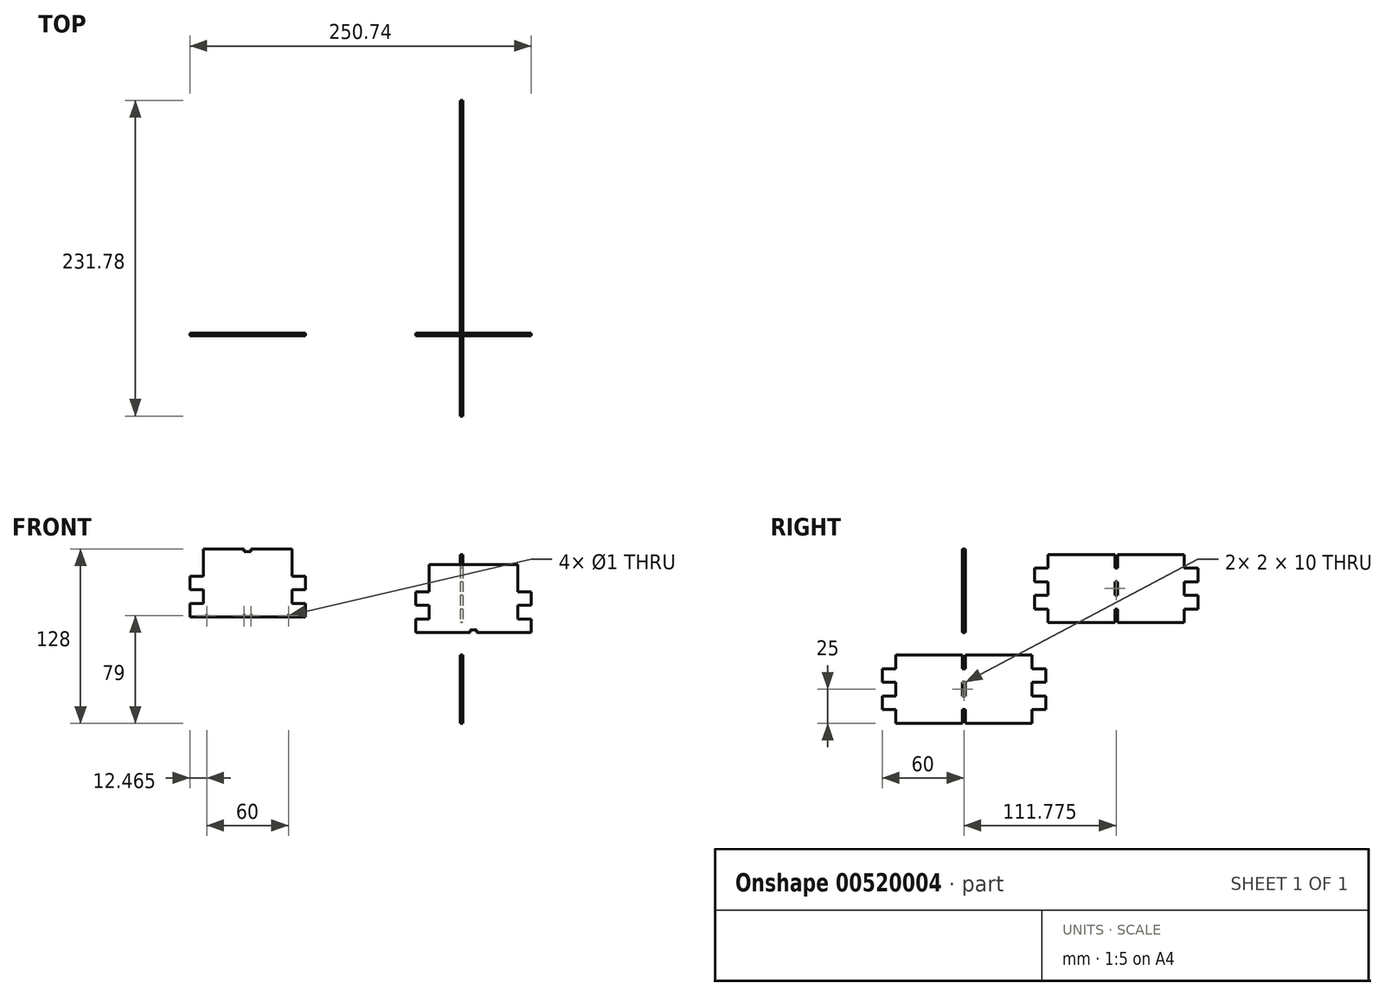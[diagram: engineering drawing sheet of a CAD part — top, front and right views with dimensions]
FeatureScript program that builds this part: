
annotation { "Feature Type Name" : "Feature", "Feature Type Description" : "" }
export const myFeature = defineFeature(function(context is Context, id is Id, definition is map)
    precondition{}
    {
        {
            var Q0;
            Q0=qCreatedBy(makeId("Front.planeOp"),FACE);
            var sketch = newSketch(context, id + "F0", { "sketchPlane" : qUnion([Q0])});
            skLineSegment(sketch, "E0.bottom", {"start": v(-198.62, 60.37) * mm, "end": v(-113.65, 60.37) * mm});
            skLineSegment(sketch, "E0.top", {"start": v(-198.62, 10.37) * mm, "end": v(-113.65, 10.37) * mm});
            skLineSegment(sketch, "E0.left", {"start": v(-198.62, 60.37) * mm, "end": v(-198.62, 10.37) * mm});
            skLineSegment(sketch, "E0.right", {"start": v(-113.65, 60.37) * mm, "end": v(-113.65, 10.37) * mm});
            skLineSegment(sketch, "E1.bottom", {"start": v(-198.62, 60.37) * mm, "end": v(-188.65, 60.37) * mm});
            skLineSegment(sketch, "E1.top", {"start": v(-198.62, 50.37) * mm, "end": v(-188.65, 50.37) * mm});
            skLineSegment(sketch, "E1.left", {"start": v(-198.62, 60.37) * mm, "end": v(-198.62, 50.37) * mm});
            skLineSegment(sketch, "E1.right", {"start": v(-188.65, 60.37) * mm, "end": v(-188.65, 50.37) * mm});
            skLineSegment(sketch, "E2.0.1.0", {"start": v(-198.62, 40.37) * mm, "end": v(-188.65, 40.37) * mm});
            skLineSegment(sketch, "E2.0.1.1", {"start": v(-198.62, 40.37) * mm, "end": v(-198.62, 30.37) * mm});
            skLineSegment(sketch, "E2.0.1.2", {"start": v(-188.65, 40.37) * mm, "end": v(-188.65, 30.37) * mm});
            skLineSegment(sketch, "E2.0.1.3", {"start": v(-198.62, 30.37) * mm, "end": v(-188.65, 30.37) * mm});
            skLineSegment(sketch, "E2.0.2.0", {"start": v(-198.62, 20.37) * mm, "end": v(-188.65, 20.37) * mm});
            skLineSegment(sketch, "E2.0.2.1", {"start": v(-198.62, 20.37) * mm, "end": v(-198.62, 10.37) * mm});
            skLineSegment(sketch, "E2.0.2.2", {"start": v(-188.65, 20.37) * mm, "end": v(-188.65, 10.37) * mm});
            skLineSegment(sketch, "E2.0.2.3", {"start": v(-198.62, 10.37) * mm, "end": v(-188.65, 10.37) * mm});
            skLineSegment(sketch, "E2.direction2", {"start": v(-198.62, 50.37) * mm, "end": v(-198.62, 30.37) * mm, "construction": true});
            skLineSegment(sketch, "E3.bottom", {"start": v(-113.65, 60.37) * mm, "end": v(-123.65, 60.37) * mm});
            skLineSegment(sketch, "E3.top", {"start": v(-113.65, 50.37) * mm, "end": v(-123.65, 50.37) * mm});
            skLineSegment(sketch, "E3.left", {"start": v(-113.65, 60.37) * mm, "end": v(-113.65, 50.37) * mm});
            skLineSegment(sketch, "E3.right", {"start": v(-123.65, 60.37) * mm, "end": v(-123.65, 50.37) * mm});
            skLineSegment(sketch, "E4.0.1.0", {"start": v(-123.65, 40.37) * mm, "end": v(-123.65, 30.37) * mm});
            skLineSegment(sketch, "E4.0.1.1", {"start": v(-113.65, 40.37) * mm, "end": v(-123.65, 40.37) * mm});
            skLineSegment(sketch, "E4.0.1.2", {"start": v(-113.65, 30.37) * mm, "end": v(-123.65, 30.37) * mm});
            skLineSegment(sketch, "E4.0.1.3", {"start": v(-113.65, 40.37) * mm, "end": v(-113.65, 30.37) * mm});
            skLineSegment(sketch, "E4.0.2.0", {"start": v(-123.65, 20.37) * mm, "end": v(-123.65, 10.37) * mm});
            skLineSegment(sketch, "E4.0.2.1", {"start": v(-113.65, 20.37) * mm, "end": v(-123.65, 20.37) * mm});
            skLineSegment(sketch, "E4.0.2.2", {"start": v(-113.65, 10.37) * mm, "end": v(-123.65, 10.37) * mm});
            skLineSegment(sketch, "E4.0.2.3", {"start": v(-113.65, 20.37) * mm, "end": v(-113.65, 10.37) * mm});
            skLineSegment(sketch, "E4.direction2", {"start": v(-123.65, 50.37) * mm, "end": v(-123.65, 30.37) * mm});
            skLineSegment(sketch, "E5", {"start": v(-188.65, 50.37) * mm, "end": v(-188.65, 40.37) * mm});
            skLineSegment(sketch, "E6", {"start": v(-188.65, 30.37) * mm, "end": v(-188.65, 20.37) * mm});
            skLineSegment(sketch, "E7", {"start": v(-123.65, 20.37) * mm, "end": v(-123.65, 30.37) * mm});
            skCircle(sketch, "E8", {"center": v(-186.15, 11.37) * mm, "radius": 0.5 * mm});
            skCircle(sketch, "E9.1.0.0", {"center": v(-158.65, 11.37) * mm, "radius": 0.5 * mm});
            skCircle(sketch, "E9.2.0.0", {"center": v(-153.65, 11.37) * mm, "radius": 0.5 * mm});
            skCircle(sketch, "E10.1.0.0", {"center": v(-126.15, 11.37) * mm, "radius": 0.5 * mm});
            skLineSegment(sketch, "E11.bottom", {"start": v(-158.65, 60.37) * mm, "end": v(-153.65, 60.37) * mm});
            skLineSegment(sketch, "E11.top", {"start": v(-158.65, 58.37) * mm, "end": v(-153.65, 58.37) * mm});
            skLineSegment(sketch, "E11.left", {"start": v(-158.65, 60.37) * mm, "end": v(-158.65, 58.37) * mm});
            skLineSegment(sketch, "E11.right", {"start": v(-153.65, 60.37) * mm, "end": v(-153.65, 58.37) * mm});
            skSolve(sketch);
        }
        {
            var Q0;
            Q0=makeQuery(id+"F0.imprint","IMPRINT",FACE,{"disambiguationData":[TD([[makeQuery(id+"F0.imprint","IMPRINT",EDGE,{"derivedFrom":sQuery(id+"F0.wireOp",EDGE,"E1.bottom")}),-1.0]])]});
            var Q1;
            Q1=makeQuery(id+"F0.imprint","IMPRINT",FACE,{"disambiguationData":[TD([[makeQuery(id+"F0.imprint","IMPRINT",EDGE,{"derivedFrom":sQuery(id+"F0.wireOp",EDGE,"E2.0.1.0")}),-1.0]])]});
            var Q2;
            Q2=makeQuery(id+"F0.imprint","IMPRINT",FACE,{"disambiguationData":[TD([[makeQuery(id+"F0.imprint","IMPRINT",EDGE,{"derivedFrom":sQuery(id+"F0.wireOp",EDGE,"E2.0.2.0")}),-1.0]])]});
            var Q3;
            Q3=makeQuery(id+"F0.imprint","IMPRINT",FACE,{"disambiguationData":[TD([[makeQuery(id+"F0.imprint","IMPRINT",EDGE,{"derivedFrom":sQuery(id+"F0.wireOp",EDGE,"E3.bottom")}),1.0]])]});
            var Q4;
            {var subQ0=sQuery(id+"F0.wireOp",EDGE,"E4.0.1.1");Q4=makeQuery(id+"F0.imprint","IMPRINT",FACE,{"disambiguationData":[TD([[makeQuery(id+"F0.imprint","IMPRINT",EDGE,{"derivedFrom":subQ0}),1.0]])]});}
            var Q5;
            Q5=makeQuery(id+"F0.imprint","IMPRINT",FACE,{"disambiguationData":[TD([[makeQuery(id+"F0.imprint","IMPRINT",EDGE,{"derivedFrom":sQuery(id+"F0.wireOp",EDGE,"E4.0.2.0")}),1.0]])]});
            var Q6;
            {var subQ6=sQuery(id+"F0.wireOp",EDGE,"E1.right");Q6=makeQuery(id+"F0.imprint","IMPRINT",FACE,{"disambiguationData":[TD([[makeQuery(id+"F0.imprint","IMPRINT",EDGE,{"derivedFrom":subQ6}),1.0]])]});}
            var Q7;
            Q7=makeQuery(id+"F0.imprint","IMPRINT",FACE,{"disambiguationData":[TD([[makeQuery(id+"F0.imprint","IMPRINT",EDGE,{"derivedFrom":sQuery(id+"F0.wireOp",EDGE,"E11.bottom")}),-1.0]])]});
            extrude(context, id + "F1", {"entities" : qUnion([Q0, Q1, Q2, Q3, Q4, Q5, Q6, Q7]), "depth" : 2 * mm, "offsetDistance" : 25 * mm});
        }
        {
            var Q0;
            Q0=qCreatedBy(makeId("Front.planeOp"),FACE);
            var sketch = newSketch(context, id + "F2", { "sketchPlane" : qUnion([Q0])});
            skLineSegment(sketch, "E12.bottom", {"start": v(-32.85, 48.9) * mm, "end": v(52.12, 48.9) * mm});
            skLineSegment(sketch, "E12.top", {"start": v(-32.85, -1.1) * mm, "end": v(52.12, -1.1) * mm});
            skLineSegment(sketch, "E12.left", {"start": v(-32.85, 48.9) * mm, "end": v(-32.85, -1.1) * mm});
            skLineSegment(sketch, "E12.right", {"start": v(52.12, 48.9) * mm, "end": v(52.12, -1.1) * mm});
            skLineSegment(sketch, "E13.bottom", {"start": v(-32.85, 48.9) * mm, "end": v(-22.88, 48.9) * mm});
            skLineSegment(sketch, "E13.top", {"start": v(-32.85, 38.9) * mm, "end": v(-22.88, 38.9) * mm});
            skLineSegment(sketch, "E13.left", {"start": v(-32.85, 48.9) * mm, "end": v(-32.85, 38.9) * mm});
            skLineSegment(sketch, "E13.right", {"start": v(-22.88, 48.9) * mm, "end": v(-22.88, 38.9) * mm});
            skLineSegment(sketch, "E14.0.1.0", {"start": v(-32.85, 28.9) * mm, "end": v(-22.88, 28.9) * mm});
            skLineSegment(sketch, "E14.0.1.1", {"start": v(-32.85, 28.9) * mm, "end": v(-32.85, 18.9) * mm});
            skLineSegment(sketch, "E14.0.1.2", {"start": v(-22.88, 28.9) * mm, "end": v(-22.88, 18.9) * mm});
            skLineSegment(sketch, "E14.0.1.3", {"start": v(-32.85, 18.9) * mm, "end": v(-22.88, 18.9) * mm});
            skLineSegment(sketch, "E14.0.2.0", {"start": v(-32.85, 8.9) * mm, "end": v(-22.88, 8.9) * mm});
            skLineSegment(sketch, "E14.0.2.1", {"start": v(-32.85, 8.9) * mm, "end": v(-32.85, -1.1) * mm});
            skLineSegment(sketch, "E14.0.2.2", {"start": v(-22.88, 8.9) * mm, "end": v(-22.88, -1.1) * mm});
            skLineSegment(sketch, "E14.0.2.3", {"start": v(-32.85, -1.1) * mm, "end": v(-22.88, -1.1) * mm});
            skLineSegment(sketch, "E14.direction2", {"start": v(-32.85, 38.9) * mm, "end": v(-32.85, 18.9) * mm, "construction": true});
            skLineSegment(sketch, "E15.bottom", {"start": v(52.12, 48.9) * mm, "end": v(42.12, 48.9) * mm});
            skLineSegment(sketch, "E15.top", {"start": v(52.12, 38.9) * mm, "end": v(42.12, 38.9) * mm});
            skLineSegment(sketch, "E15.left", {"start": v(52.12, 48.9) * mm, "end": v(52.12, 38.9) * mm});
            skLineSegment(sketch, "E15.right", {"start": v(42.12, 48.9) * mm, "end": v(42.12, 38.9) * mm});
            skLineSegment(sketch, "E16.0.1.0", {"start": v(42.12, 28.9) * mm, "end": v(42.12, 18.9) * mm});
            skLineSegment(sketch, "E16.0.1.1", {"start": v(52.12, 28.9) * mm, "end": v(42.12, 28.9) * mm});
            skLineSegment(sketch, "E16.0.1.2", {"start": v(52.12, 18.9) * mm, "end": v(42.12, 18.9) * mm});
            skLineSegment(sketch, "E16.0.1.3", {"start": v(52.12, 28.9) * mm, "end": v(52.12, 18.9) * mm});
            skLineSegment(sketch, "E16.0.2.0", {"start": v(42.12, 8.9) * mm, "end": v(42.12, -1.1) * mm});
            skLineSegment(sketch, "E16.0.2.1", {"start": v(52.12, 8.9) * mm, "end": v(42.12, 8.9) * mm});
            skLineSegment(sketch, "E16.0.2.2", {"start": v(52.12, -1.1) * mm, "end": v(42.12, -1.1) * mm});
            skLineSegment(sketch, "E16.0.2.3", {"start": v(52.12, 8.9) * mm, "end": v(52.12, -1.1) * mm});
            skLineSegment(sketch, "E16.direction2", {"start": v(42.12, 38.9) * mm, "end": v(42.12, 18.9) * mm});
            skLineSegment(sketch, "E17", {"start": v(-22.88, 38.9) * mm, "end": v(-22.88, 28.9) * mm});
            skLineSegment(sketch, "E18", {"start": v(-22.88, 18.9) * mm, "end": v(-22.88, 8.9) * mm});
            skLineSegment(sketch, "E19", {"start": v(42.12, 8.9) * mm, "end": v(42.12, 18.9) * mm});
            skCircle(sketch, "E20", {"center": v(-20.38, 3.9) * mm, "radius": 0.5 * mm});
            skCircle(sketch, "E21.1.0.0", {"center": v(7.12, 3.9) * mm, "radius": 0.5 * mm});
            skCircle(sketch, "E21.2.0.0", {"center": v(12.12, 3.9) * mm, "radius": 0.5 * mm});
            skCircle(sketch, "E22.1.0.0", {"center": v(39.62, 3.9) * mm, "radius": 0.5 * mm});
            skLineSegment(sketch, "E23.bottom", {"start": v(7.12, 48.9) * mm, "end": v(12.12, 48.9) * mm});
            skLineSegment(sketch, "E24.bottom", {"start": v(7.12, 0.9) * mm, "end": v(12.12, 0.9) * mm});
            skLineSegment(sketch, "E24.top", {"start": v(7.12, -1.1) * mm, "end": v(12.12, -1.1) * mm});
            skLineSegment(sketch, "E24.left", {"start": v(7.12, 0.9) * mm, "end": v(7.12, -1.1) * mm});
            skLineSegment(sketch, "E24.right", {"start": v(12.12, 0.9) * mm, "end": v(12.12, -1.1) * mm});
            skSolve(sketch);
        }
        {
            var Q0;
            {var subQ6=sQuery(id+"F2.wireOp",EDGE,"E13.right");Q0=makeQuery(id+"F2.imprint","IMPRINT",FACE,{"disambiguationData":[TD([[makeQuery(id+"F2.imprint","IMPRINT",EDGE,{"derivedFrom":subQ6}),1.0]])]});}
            var Q1;
            Q1=makeQuery(id+"F2.imprint","IMPRINT",FACE,{"disambiguationData":[TD([[makeQuery(id+"F2.imprint","IMPRINT",EDGE,{"derivedFrom":sQuery(id+"F2.wireOp",EDGE,"E15.bottom")}),1.0]])]});
            var Q2;
            {var subQ0=sQuery(id+"F2.wireOp",EDGE,"E16.0.1.1");Q2=makeQuery(id+"F2.imprint","IMPRINT",FACE,{"disambiguationData":[TD([[makeQuery(id+"F2.imprint","IMPRINT",EDGE,{"derivedFrom":subQ0}),1.0]])]});}
            var Q3;
            Q3=makeQuery(id+"F2.imprint","IMPRINT",FACE,{"disambiguationData":[TD([[makeQuery(id+"F2.imprint","IMPRINT",EDGE,{"derivedFrom":sQuery(id+"F2.wireOp",EDGE,"E16.0.2.0")}),1.0]])]});
            var Q4;
            Q4=makeQuery(id+"F2.imprint","IMPRINT",FACE,{"disambiguationData":[TD([[makeQuery(id+"F2.imprint","IMPRINT",EDGE,{"derivedFrom":sQuery(id+"F2.wireOp",EDGE,"E13.bottom")}),-1.0]])]});
            var Q5;
            Q5=makeQuery(id+"F2.imprint","IMPRINT",FACE,{"disambiguationData":[TD([[makeQuery(id+"F2.imprint","IMPRINT",EDGE,{"derivedFrom":sQuery(id+"F2.wireOp",EDGE,"E14.0.1.0")}),-1.0]])]});
            var Q6;
            Q6=makeQuery(id+"F2.imprint","IMPRINT",FACE,{"disambiguationData":[TD([[makeQuery(id+"F2.imprint","IMPRINT",EDGE,{"derivedFrom":sQuery(id+"F2.wireOp",EDGE,"E14.0.2.0")}),-1.0]])]});
            var Q7;
            Q7=makeQuery(id+"F2.imprint","IMPRINT",FACE,{"disambiguationData":[TD([[makeQuery(id+"F2.imprint","IMPRINT",EDGE,{"derivedFrom":sQuery(id+"F2.wireOp",EDGE,"E20")}),1.0]])]});
            var Q8;
            Q8=makeQuery(id+"F2.imprint","IMPRINT",FACE,{"disambiguationData":[TD([[makeQuery(id+"F2.imprint","IMPRINT",EDGE,{"derivedFrom":sQuery(id+"F2.wireOp",EDGE,"E21.1.0.0")}),1.0]])]});
            var Q9;
            Q9=makeQuery(id+"F2.imprint","IMPRINT",FACE,{"disambiguationData":[TD([[makeQuery(id+"F2.imprint","IMPRINT",EDGE,{"derivedFrom":sQuery(id+"F2.wireOp",EDGE,"E21.2.0.0")}),1.0]])]});
            var Q10;
            Q10=makeQuery(id+"F2.imprint","IMPRINT",FACE,{"disambiguationData":[TD([[makeQuery(id+"F2.imprint","IMPRINT",EDGE,{"derivedFrom":sQuery(id+"F2.wireOp",EDGE,"E22.1.0.0")}),1.0]])]});
            extrude(context, id + "F3", {"entities" : qUnion([Q0, Q1, Q2, Q3, Q4, Q5, Q6, Q7, Q8, Q9, Q10]), "depth" : 2 * mm, "offsetDistance" : 25 * mm});
        }
        {
            var Q0;
            Q0=qCreatedBy(makeId("Right.planeOp"),FACE);
            var sketch = newSketch(context, id + "F4", { "sketchPlane" : qUnion([Q0])});
            skLineSegment(sketch, "E25.bottom", {"start": v(-51, -17.63) * mm, "end": v(49, -17.63) * mm});
            skLineSegment(sketch, "E25.top", {"start": v(-51, -67.63) * mm, "end": v(49, -67.63) * mm});
            skLineSegment(sketch, "E25.left", {"start": v(-51, -17.63) * mm, "end": v(-51, -67.63) * mm});
            skLineSegment(sketch, "E25.right", {"start": v(49, -17.63) * mm, "end": v(49, -67.63) * mm});
            skLineSegment(sketch, "E26.bottom", {"start": v(-2, -17.63) * mm, "end": v(0, -17.63) * mm});
            skLineSegment(sketch, "E26.top", {"start": v(-2, -27.63) * mm, "end": v(0, -27.63) * mm});
            skLineSegment(sketch, "E26.left", {"start": v(-2, -17.63) * mm, "end": v(-2, -27.63) * mm});
            skLineSegment(sketch, "E26.right", {"start": v(0, -17.63) * mm, "end": v(0, -27.63) * mm});
            skLineSegment(sketch, "E27.0.1.0", {"start": v(-2, -47.63) * mm, "end": v(0, -47.63) * mm});
            skLineSegment(sketch, "E27.0.1.1", {"start": v(-2, -37.63) * mm, "end": v(-2, -47.63) * mm});
            skLineSegment(sketch, "E27.0.1.2", {"start": v(0, -37.63) * mm, "end": v(0, -47.63) * mm});
            skLineSegment(sketch, "E27.0.1.3", {"start": v(-2, -37.63) * mm, "end": v(0, -37.63) * mm});
            skLineSegment(sketch, "E27.0.2.0", {"start": v(-2, -67.63) * mm, "end": v(0, -67.63) * mm});
            skLineSegment(sketch, "E27.0.2.1", {"start": v(-2, -57.63) * mm, "end": v(-2, -67.63) * mm});
            skLineSegment(sketch, "E27.0.2.2", {"start": v(0, -57.63) * mm, "end": v(0, -67.63) * mm});
            skLineSegment(sketch, "E27.0.2.3", {"start": v(-2, -57.63) * mm, "end": v(0, -57.63) * mm});
            skLineSegment(sketch, "E27.direction1", {"start": v(-2, -27.63) * mm, "end": v(-0.14, -27.63) * mm, "construction": true});
            skLineSegment(sketch, "E28.bottom", {"start": v(49, -17.63) * mm, "end": v(59, -17.63) * mm});
            skLineSegment(sketch, "E28.top", {"start": v(49, -27.63) * mm, "end": v(59, -27.63) * mm});
            skLineSegment(sketch, "E28.left", {"start": v(49, -17.63) * mm, "end": v(49, -27.63) * mm});
            skLineSegment(sketch, "E28.right", {"start": v(59, -17.63) * mm, "end": v(59, -27.63) * mm});
            skLineSegment(sketch, "E29.0.1.0", {"start": v(59, -37.63) * mm, "end": v(59, -47.63) * mm});
            skLineSegment(sketch, "E29.0.1.1", {"start": v(49, -47.63) * mm, "end": v(59, -47.63) * mm});
            skLineSegment(sketch, "E29.0.1.2", {"start": v(49, -37.63) * mm, "end": v(49, -47.63) * mm});
            skLineSegment(sketch, "E29.0.1.3", {"start": v(49, -37.63) * mm, "end": v(59, -37.63) * mm});
            skLineSegment(sketch, "E29.0.2.0", {"start": v(59, -57.63) * mm, "end": v(59, -67.63) * mm});
            skLineSegment(sketch, "E29.0.2.1", {"start": v(49, -67.63) * mm, "end": v(59, -67.63) * mm});
            skLineSegment(sketch, "E29.0.2.2", {"start": v(49, -57.63) * mm, "end": v(49, -67.63) * mm});
            skLineSegment(sketch, "E29.0.2.3", {"start": v(49, -57.63) * mm, "end": v(59, -57.63) * mm});
            skLineSegment(sketch, "E29.direction2", {"start": v(49, -27.63) * mm, "end": v(49, -47.63) * mm, "construction": true});
            skLineSegment(sketch, "E30.bottom", {"start": v(-51, -17.63) * mm, "end": v(-61, -17.63) * mm});
            skLineSegment(sketch, "E30.top", {"start": v(-51, -27.63) * mm, "end": v(-61, -27.63) * mm});
            skLineSegment(sketch, "E30.left", {"start": v(-51, -17.63) * mm, "end": v(-51, -27.63) * mm});
            skLineSegment(sketch, "E30.right", {"start": v(-61, -17.63) * mm, "end": v(-61, -27.63) * mm});
            skLineSegment(sketch, "E31.0.1.0", {"start": v(-51, -37.63) * mm, "end": v(-51, -47.63) * mm});
            skLineSegment(sketch, "E31.0.1.1", {"start": v(-51, -47.63) * mm, "end": v(-61, -47.63) * mm});
            skLineSegment(sketch, "E31.0.1.2", {"start": v(-51, -37.63) * mm, "end": v(-61, -37.63) * mm});
            skLineSegment(sketch, "E31.0.1.3", {"start": v(-61, -37.63) * mm, "end": v(-61, -47.63) * mm});
            skLineSegment(sketch, "E31.0.2.0", {"start": v(-51, -57.63) * mm, "end": v(-51, -67.63) * mm});
            skLineSegment(sketch, "E31.0.2.1", {"start": v(-51, -67.63) * mm, "end": v(-61, -67.63) * mm});
            skLineSegment(sketch, "E31.0.2.2", {"start": v(-51, -57.63) * mm, "end": v(-61, -57.63) * mm});
            skLineSegment(sketch, "E31.0.2.3", {"start": v(-61, -57.63) * mm, "end": v(-61, -67.63) * mm});
            skLineSegment(sketch, "E32", {"start": v(-61, -27.63) * mm, "end": v(-61, -37.63) * mm});
            skLineSegment(sketch, "E33", {"start": v(-61, -47.63) * mm, "end": v(-61, -57.63) * mm});
            skLineSegment(sketch, "E34", {"start": v(59, -27.63) * mm, "end": v(59, -37.63) * mm});
            skLineSegment(sketch, "E35", {"start": v(59, -47.63) * mm, "end": v(59, -57.63) * mm});
            skSolve(sketch);
        }
        {
            var Q0;
            {var subQ0=sQuery(id+"F4.wireOp",EDGE,"E30.top");Q0=makeQuery(id+"F4.imprint","IMPRINT",FACE,{"disambiguationData":[TD([[makeQuery(id+"F4.imprint","IMPRINT",EDGE,{"derivedFrom":subQ0}),1.0]])]});}
            var Q1;
            {var subQ2=sQuery(id+"F4.wireOp",EDGE,"E31.0.1.1");Q1=makeQuery(id+"F4.imprint","IMPRINT",FACE,{"disambiguationData":[TD([[makeQuery(id+"F4.imprint","IMPRINT",EDGE,{"derivedFrom":subQ2}),1.0]])]});}
            var Q2;
            {var subQ0=sQuery(id+"F4.wireOp",EDGE,"E28.top");Q2=makeQuery(id+"F4.imprint","IMPRINT",FACE,{"disambiguationData":[TD([[makeQuery(id+"F4.imprint","IMPRINT",EDGE,{"derivedFrom":subQ0}),-1.0]])]});}
            var Q3;
            {var subQ2=sQuery(id+"F4.wireOp",EDGE,"E29.0.1.1");Q3=makeQuery(id+"F4.imprint","IMPRINT",FACE,{"disambiguationData":[TD([[makeQuery(id+"F4.imprint","IMPRINT",EDGE,{"derivedFrom":subQ2}),-1.0]])]});}
            var Q4;
            Q4=makeQuery(id+"F4.imprint","IMPRINT",FACE,{"disambiguationData":[TD([[makeQuery(id+"F4.imprint","IMPRINT",EDGE,{"derivedFrom":sQuery(id+"F4.wireOp",EDGE,"E26.top")}),-1.0]])]});
            extrude(context, id + "F5", {"entities" : qUnion([Q0, Q1, Q2, Q3, Q4]), "depth" : 2 * mm, "offsetDistance" : 25 * mm});
        }
        {
            var Q0;
            Q0=qCreatedBy(makeId("Right.planeOp"),FACE);
            var sketch = newSketch(context, id + "F6", { "sketchPlane" : qUnion([Q0])});
            skLineSegment(sketch, "E36.bottom", {"start": v(60.78, 56.3) * mm, "end": v(160.78, 56.3) * mm});
            skLineSegment(sketch, "E36.top", {"start": v(60.78, 6.3) * mm, "end": v(160.78, 6.3) * mm});
            skLineSegment(sketch, "E36.left", {"start": v(60.78, 56.3) * mm, "end": v(60.78, 6.3) * mm});
            skLineSegment(sketch, "E36.right", {"start": v(160.78, 56.3) * mm, "end": v(160.78, 6.3) * mm});
            skLineSegment(sketch, "E37.bottom", {"start": v(109.78, 56.3) * mm, "end": v(111.78, 56.3) * mm});
            skLineSegment(sketch, "E37.top", {"start": v(109.78, 46.3) * mm, "end": v(111.78, 46.3) * mm});
            skLineSegment(sketch, "E37.left", {"start": v(109.78, 56.3) * mm, "end": v(109.78, 46.3) * mm});
            skLineSegment(sketch, "E37.right", {"start": v(111.78, 56.3) * mm, "end": v(111.78, 46.3) * mm});
            skLineSegment(sketch, "E38.0.1.0", {"start": v(109.78, 26.3) * mm, "end": v(111.78, 26.3) * mm});
            skLineSegment(sketch, "E38.0.1.1", {"start": v(109.78, 36.3) * mm, "end": v(109.78, 26.3) * mm});
            skLineSegment(sketch, "E38.0.1.2", {"start": v(111.78, 36.3) * mm, "end": v(111.78, 26.3) * mm});
            skLineSegment(sketch, "E38.0.1.3", {"start": v(109.78, 36.3) * mm, "end": v(111.78, 36.3) * mm});
            skLineSegment(sketch, "E38.0.2.0", {"start": v(109.78, 6.3) * mm, "end": v(111.78, 6.3) * mm});
            skLineSegment(sketch, "E38.0.2.1", {"start": v(109.78, 16.3) * mm, "end": v(109.78, 6.3) * mm});
            skLineSegment(sketch, "E38.0.2.2", {"start": v(111.78, 16.3) * mm, "end": v(111.78, 6.3) * mm});
            skLineSegment(sketch, "E38.0.2.3", {"start": v(109.78, 16.3) * mm, "end": v(111.78, 16.3) * mm});
            skLineSegment(sketch, "E38.direction1", {"start": v(56.9, 46.3) * mm, "end": v(109.78, 46.3) * mm, "construction": true});
            skLineSegment(sketch, "E39.bottom", {"start": v(160.78, 56.3) * mm, "end": v(170.78, 56.3) * mm});
            skLineSegment(sketch, "E39.top", {"start": v(160.78, 46.3) * mm, "end": v(170.78, 46.3) * mm});
            skLineSegment(sketch, "E39.left", {"start": v(160.78, 56.3) * mm, "end": v(160.78, 46.3) * mm});
            skLineSegment(sketch, "E39.right", {"start": v(170.78, 56.3) * mm, "end": v(170.78, 46.3) * mm});
            skLineSegment(sketch, "E40.0.1.0", {"start": v(170.78, 36.3) * mm, "end": v(170.78, 26.3) * mm});
            skLineSegment(sketch, "E40.0.1.1", {"start": v(160.78, 26.3) * mm, "end": v(170.78, 26.3) * mm});
            skLineSegment(sketch, "E40.0.1.2", {"start": v(160.78, 36.3) * mm, "end": v(160.78, 26.3) * mm});
            skLineSegment(sketch, "E40.0.1.3", {"start": v(160.78, 36.3) * mm, "end": v(170.78, 36.3) * mm});
            skLineSegment(sketch, "E40.0.2.0", {"start": v(170.78, 16.3) * mm, "end": v(170.78, 6.3) * mm});
            skLineSegment(sketch, "E40.0.2.1", {"start": v(160.78, 6.3) * mm, "end": v(170.78, 6.3) * mm});
            skLineSegment(sketch, "E40.0.2.2", {"start": v(160.78, 16.3) * mm, "end": v(160.78, 6.3) * mm});
            skLineSegment(sketch, "E40.0.2.3", {"start": v(160.78, 16.3) * mm, "end": v(170.78, 16.3) * mm});
            skLineSegment(sketch, "E40.direction2", {"start": v(160.78, 46.3) * mm, "end": v(160.78, 26.3) * mm, "construction": true});
            skLineSegment(sketch, "E41.bottom", {"start": v(60.78, 56.3) * mm, "end": v(50.78, 56.3) * mm});
            skLineSegment(sketch, "E41.top", {"start": v(60.78, 46.3) * mm, "end": v(50.78, 46.3) * mm});
            skLineSegment(sketch, "E41.left", {"start": v(60.78, 56.3) * mm, "end": v(60.78, 46.3) * mm});
            skLineSegment(sketch, "E41.right", {"start": v(50.78, 56.3) * mm, "end": v(50.78, 46.3) * mm});
            skLineSegment(sketch, "E42.0.1.0", {"start": v(60.78, 36.3) * mm, "end": v(60.78, 26.3) * mm});
            skLineSegment(sketch, "E42.0.1.1", {"start": v(60.78, 26.3) * mm, "end": v(50.78, 26.3) * mm});
            skLineSegment(sketch, "E42.0.1.2", {"start": v(60.78, 36.3) * mm, "end": v(50.78, 36.3) * mm});
            skLineSegment(sketch, "E42.0.1.3", {"start": v(50.78, 36.3) * mm, "end": v(50.78, 26.3) * mm});
            skLineSegment(sketch, "E42.0.2.0", {"start": v(60.78, 16.3) * mm, "end": v(60.78, 6.3) * mm});
            skLineSegment(sketch, "E42.0.2.1", {"start": v(60.78, 6.3) * mm, "end": v(50.78, 6.3) * mm});
            skLineSegment(sketch, "E42.0.2.2", {"start": v(60.78, 16.3) * mm, "end": v(50.78, 16.3) * mm});
            skLineSegment(sketch, "E42.0.2.3", {"start": v(50.78, 16.3) * mm, "end": v(50.78, 6.3) * mm});
            skLineSegment(sketch, "E43", {"start": v(50.78, 46.3) * mm, "end": v(50.78, 36.3) * mm});
            skLineSegment(sketch, "E44", {"start": v(50.78, 26.3) * mm, "end": v(50.78, 16.3) * mm});
            skLineSegment(sketch, "E45", {"start": v(170.78, 46.3) * mm, "end": v(170.78, 36.3) * mm});
            skLineSegment(sketch, "E46", {"start": v(170.78, 26.3) * mm, "end": v(170.78, 16.3) * mm});
            skSolve(sketch);
        }
        {
            var Q0;
            {var subQ0=sQuery(id+"F6.wireOp",EDGE,"E41.top");Q0=makeQuery(id+"F6.imprint","IMPRINT",FACE,{"disambiguationData":[TD([[makeQuery(id+"F6.imprint","IMPRINT",EDGE,{"derivedFrom":subQ0}),1.0]])]});}
            var Q1;
            {var subQ2=sQuery(id+"F6.wireOp",EDGE,"E42.0.1.1");Q1=makeQuery(id+"F6.imprint","IMPRINT",FACE,{"disambiguationData":[TD([[makeQuery(id+"F6.imprint","IMPRINT",EDGE,{"derivedFrom":subQ2}),1.0]])]});}
            var Q2;
            {var subQ0=sQuery(id+"F6.wireOp",EDGE,"E39.top");Q2=makeQuery(id+"F6.imprint","IMPRINT",FACE,{"disambiguationData":[TD([[makeQuery(id+"F6.imprint","IMPRINT",EDGE,{"derivedFrom":subQ0}),-1.0]])]});}
            var Q3;
            {var subQ2=sQuery(id+"F6.wireOp",EDGE,"E40.0.1.1");Q3=makeQuery(id+"F6.imprint","IMPRINT",FACE,{"disambiguationData":[TD([[makeQuery(id+"F6.imprint","IMPRINT",EDGE,{"derivedFrom":subQ2}),-1.0]])]});}
            var Q4;
            Q4=makeQuery(id+"F6.imprint","IMPRINT",FACE,{"disambiguationData":[TD([[makeQuery(id+"F6.imprint","IMPRINT",EDGE,{"derivedFrom":sQuery(id+"F6.wireOp",EDGE,"E37.top")}),-1.0]])]});
            extrude(context, id + "F7", {"entities" : qUnion([Q0, Q1, Q2, Q3, Q4]), "operationType" : NewBodyOperationType.ADD, "depth" : 2 * mm, "offsetDistance" : 25 * mm});
        }
    });
